# Revit family: Lustro_dla_zakładow_karnych 700 x 500 mm
name_source: partatom
category: Furniture
units: mm (PartAtom-declared; Revit-internal decimal feet)

## family parameters
Always vertical = Yes
Cut with Voids When Loaded = No
Host = Wall
Room Calculation Point = No
Shared = No

## types (1)
- N08071
    Depth / Glebokosc = 1 mm  [stored 0.00328084 ft]
    Description = Lustro przeznaczone do zakładów penitencjarnych wykonane jest ze stali nierdzewnej polerowanej. Jest bardzo odporne na wszelkie akty wandalizmu, dlatego idealnie nadaje się do montażu w więzieniach. Lustro stalowe nie ulega stłuczeniu, co zapewnia wysokie bezpieczeństwo użytkowania.
    Height / Wysokosc = 700 mm  [stored 2.29659 ft]
    Lustro = Stal nierdzewna AISI 304 polerowana
    Manufacturer = FANECO.com
    Manufacturer code / Kod producenta = 5901764294665
    Material finish / Wykonczenie = Stal nierdzewna 304 polerowana
    Product code / Kod produktu = N08071
    Type Comments = Lustro dla zakładów karnych 700 x 500 mm stal szlachetna połysk
    URL = https://faneco.com
    Width / Szerokosc = 500 mm  [stored 1.64042 ft]

note: [stored X ft] marks values corroborated as IEEE doubles in the binary element streams (Revit-internal decimal feet)

## geometry (parser evidence)
native form markers: Sweep x5
no freeform markers — native parametric forms only
